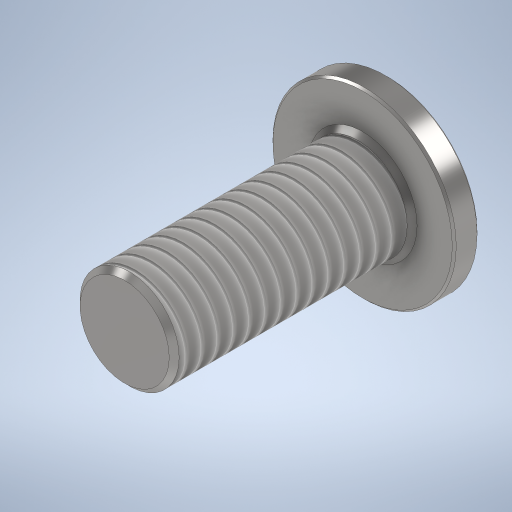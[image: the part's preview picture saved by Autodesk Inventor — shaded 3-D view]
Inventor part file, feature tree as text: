
AUTODESK INVENTOR PART (.ipt)
format: ipt  version: 2024 (Build 280153000, 153)  size: 374,784 bytes
history: native  units: mm
features: extrude x3, chamfer x3, sketch x2, thread x1, hole x1
ambient origin geometry x8: Origin, YZ Plane, XZ Plane, XY Plane, X Axis, Y Axis, Z Axis, Center Point
bodies: Solid1 (feature_tree)
feature tree (10):
  sketch  "Sketch1"  dims[d0=9.25mm d1=5.0mm]
  extrude  "Extrusion1"  Depth=5.0mm
  extrude  "Extrusion2"  Depth=2.5mm TaperAngle=0.0deg
  thread  "Thread1"  [1 undecoded]
  chamfer  "Chamfer1"  Distance=0.1mm Angle=45.0deg
  sketch  "Sketch2"  dims[d2=12.0mm d3=0.0mm d4=1.25mm d5=0.0mm d6=15.0mm d7=0.0mm d8=0.1mm d9=2.0mm d10=45.0deg d11=3.75mm d15=0.5mm d16=0.8mm d17=45.0deg d18=3.0mm d19=0.0mm d20=0.25mm d21=2.0mm d22=45.0deg d23=2.5mm d24=6.0mm d25=4.0mm d26=2.0mm d27=90.0deg d28=2.5mm d29=150.0deg d30=3.94mm d31=0.66mm d32=1.66mm d33=2.5mm]
  hole  "Hole1"  [1 undecoded]
  chamfer  "Chamfer2"  Distance=3.0mm
  extrude  "Extrusion4"  Depth=2.5mm TaperAngle=45.0deg
  chamfer  "Chamfer3"  Distance=2.5mm
note: 2 required parameter values undecoded (feature->parameter linkage not recoverable at this tier; creation-order binding heuristic only, values carry confidence <= 0.55)
